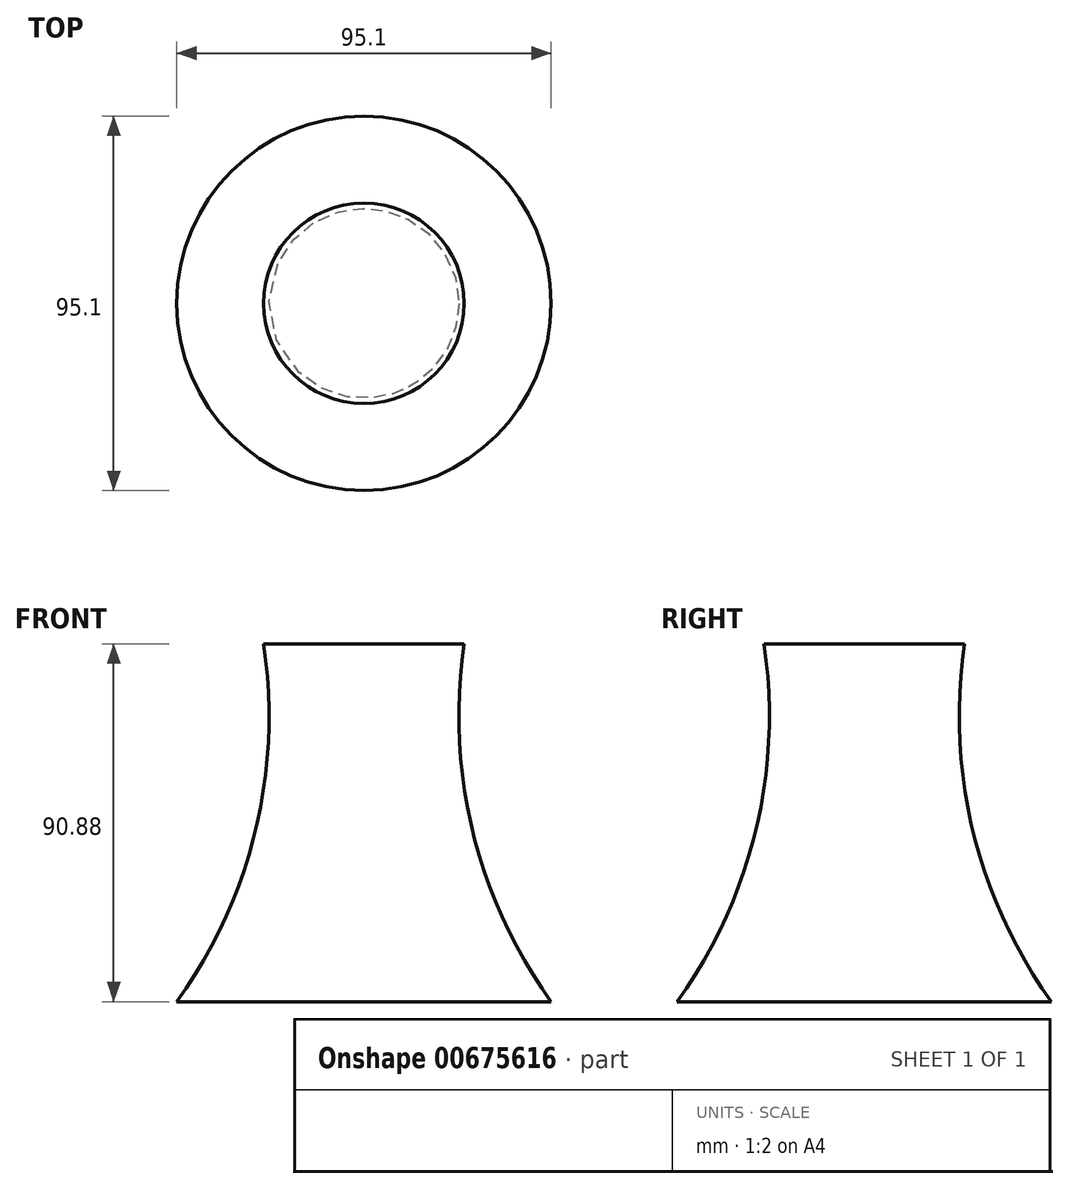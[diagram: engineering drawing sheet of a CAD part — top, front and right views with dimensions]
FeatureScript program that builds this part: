
annotation { "Feature Type Name" : "Feature", "Feature Type Description" : "" }
export const myFeature = defineFeature(function(context is Context, id is Id, definition is map)
    precondition{}
    {
        {
            var Q0;
            Q0=qCreatedBy(makeId("Front.planeOp"),FACE);
            var sketch = newSketch(context, id + "F0", { "sketchPlane" : qUnion([Q0])});
            skArc(sketch, "E0", {"start": v(-47.55, -48.36) * mm, "mid": v(-27.63, -5.08) * mm, "end": v(-25.48, 42.52) * mm});
            skLineSegment(sketch, "E1", {"start": v(-25.48, 42.52) * mm, "end": v(0, 42.52) * mm});
            skLineSegment(sketch, "E2", {"start": v(0, 42.52) * mm, "end": v(0, -48.36) * mm});
            skLineSegment(sketch, "E3", {"start": v(0, -48.36) * mm, "end": v(-47.55, -48.36) * mm});
            skSolve(sketch);
        }
        {
            var Q0;
            Q0=makeQuery(id+"F0.imprint","IMPRINT",FACE,{"disambiguationData":[TD([[makeQuery(id+"F0.imprint","IMPRINT",EDGE,{"derivedFrom":sQuery(id+"F0.wireOp",EDGE,"E0")}),-1.0]])]});
            var Q1;
            Q1=sQuery(id+"F0.wireOp",EDGE,"E2");
            revolve(context, id + "F1", {"entities" : qUnion([Q0]), "axis" : qUnion([Q1]), "revolveType" : RevolveType.FULL});
        }
    });
